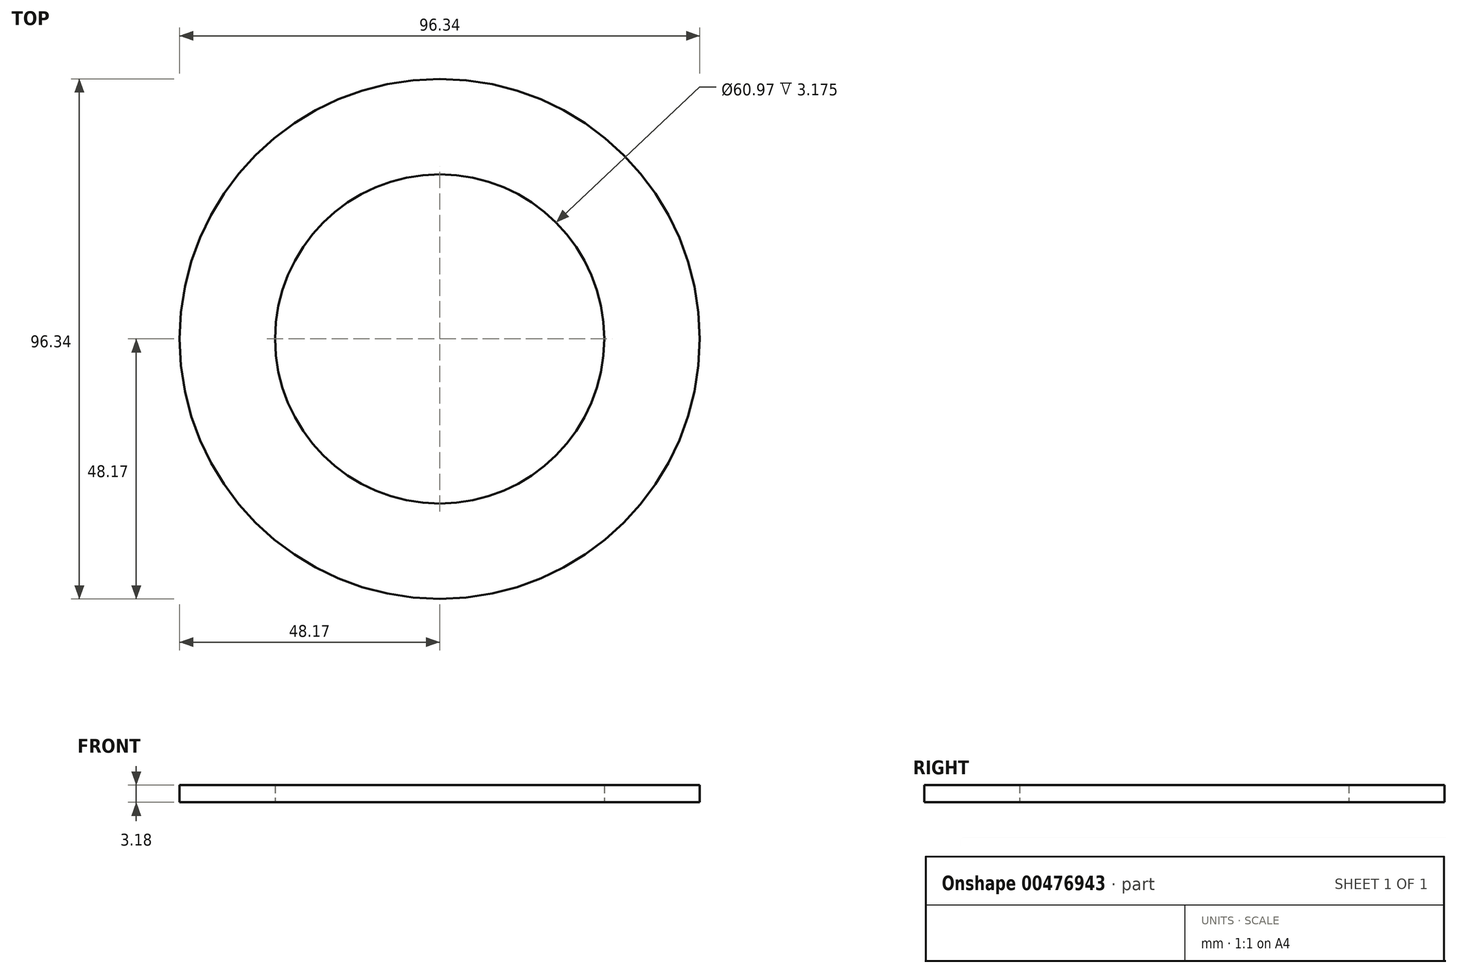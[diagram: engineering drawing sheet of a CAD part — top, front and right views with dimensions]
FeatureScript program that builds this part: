
annotation { "Feature Type Name" : "Feature", "Feature Type Description" : "" }
export const myFeature = defineFeature(function(context is Context, id is Id, definition is map)
    precondition{}
    {
        {
            var Q0;
            Q0=qCreatedBy(makeId("Top.planeOp"),FACE);
            var sketch = newSketch(context, id + "F0", { "sketchPlane" : qUnion([Q0])});
            skCircle(sketch, "E0", {"center": v(0, 0) * mm, "radius": 48.17 * mm});
            skCircle(sketch, "E1", {"center": v(0, 0) * mm, "radius": 30.49 * mm});
            skSolve(sketch);
        }
        {
            var Q0;
            Q0 = qSketchRegion(id + "F0", true);
            extrude(context, id + "F1", {"entities" : qUnion([Q0]), "depth" : 3.17 * mm});
        }
    });
